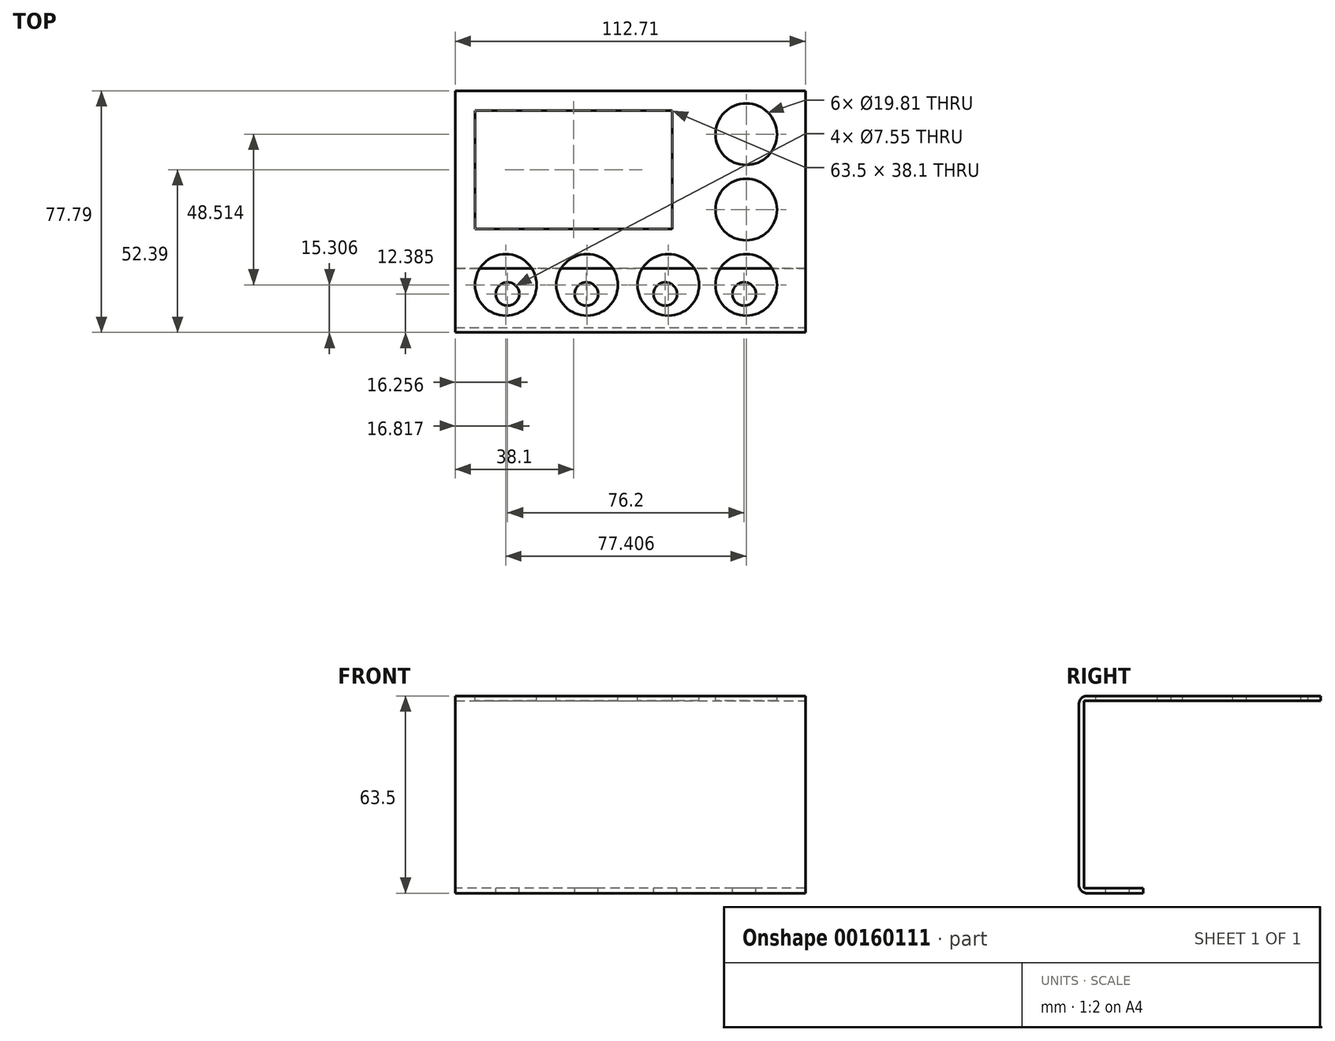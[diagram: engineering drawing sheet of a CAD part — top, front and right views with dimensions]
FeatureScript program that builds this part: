
annotation { "Feature Type Name" : "Feature", "Feature Type Description" : "" }
export const myFeature = defineFeature(function(context is Context, id is Id, definition is map)
    precondition{}
    {
        {
            var Q0;
            Q0=qCreatedBy(makeId("Top.planeOp"),FACE);
            var sketch = newSketch(context, id + "F0", { "sketchPlane" : qUnion([Q0])});
            skLineSegment(sketch, "E0.bottom", {"start": v(-56.35, 38.1) * mm, "end": v(56.36, 38.1) * mm});
            skLineSegment(sketch, "E0.top", {"start": v(-56.35, -38.1) * mm, "end": v(56.36, -38.1) * mm});
            skLineSegment(sketch, "E0.left", {"start": v(-56.35, 38.1) * mm, "end": v(-56.35, -38.1) * mm});
            skLineSegment(sketch, "E0.right", {"start": v(56.36, 38.1) * mm, "end": v(56.36, -38.1) * mm});
            skSolve(sketch);
        }
        {
            var Q0;
            Q0=makeQuery(id+"F0.imprint","IMPRINT",FACE,{"disambiguationData":[TD([[makeQuery(id+"F0.imprint","IMPRINT",EDGE,{"derivedFrom":sQuery(id+"F0.wireOp",EDGE,"E0.bottom")}),-1.0]])]});
            extrude(context, id + "F1", {"entities" : qUnion([Q0]), "depth" : 1.59 * mm});
        }
        {
            var Q0;
            Q0=makeQuery(id+"F1.opExtrude","CAP_FACE",FACE,{"disambiguationData":[OSD([sQuery(id+"F0.wireOp",EDGE,"E0.bottom"),sQuery(id+"F0.wireOp",EDGE,"E0.top"),sQuery(id+"F0.wireOp",EDGE,"E0.left"),sQuery(id+"F0.wireOp",EDGE,"E0.right")])],"isStart":false});
            var sketch = newSketch(context, id + "F2", { "sketchPlane" : qUnion([Q0])});
            skLineSegment(sketch, "E1.bottom", {"start": v(-50, 31.75) * mm, "end": v(13.5, 31.75) * mm});
            skLineSegment(sketch, "E1.top", {"start": v(-50, -6.35) * mm, "end": v(13.5, -6.35) * mm});
            skLineSegment(sketch, "E1.left", {"start": v(-50, 31.75) * mm, "end": v(-50, -6.35) * mm});
            skLineSegment(sketch, "E1.right", {"start": v(13.5, 31.75) * mm, "end": v(13.5, -6.35) * mm});
            skCircle(sketch, "E2", {"center": v(37.31, 24.13) * mm, "radius": 9.9 * mm});
            skCircle(sketch, "E3", {"center": v(37.31, -0.13) * mm, "radius": 9.9 * mm});
            skCircle(sketch, "E4", {"center": v(37.31, -24.38) * mm, "radius": 9.9 * mm});
            skLineSegment(sketch, "E5", {"start": v(37.31, 38.1) * mm, "end": v(37.31, -38.1) * mm, "construction": true});
            skLineSegment(sketch, "E6", {"start": v(37.31, -24.38) * mm, "end": v(-56.35, -24.38) * mm, "construction": true});
            skCircle(sketch, "E7", {"center": v(-40.1, -24.38) * mm, "radius": 9.9 * mm});
            skCircle(sketch, "E8", {"center": v(-13.93, -24.38) * mm, "radius": 9.9 * mm});
            skCircle(sketch, "E9", {"center": v(12.23, -24.38) * mm, "radius": 9.9 * mm});
            skSolve(sketch);
        }
        {
            var Q0;
            Q0 = qSketchRegion(id + "F2", true);
            extrude(context, id + "F3", {"entities" : qUnion([Q0]), "operationType" : NewBodyOperationType.REMOVE, "endBound" : BoundingType.THROUGH_ALL, "oppositeDirection" : true, "depth" : 25.4 * mm});
        }
        {
            var Q0;
            Q0=makeQuery(id+"F1.opExtrude","CAP_FACE",FACE,{"disambiguationData":[OSD([sQuery(id+"F0.wireOp",EDGE,"E0.bottom"),sQuery(id+"F0.wireOp",EDGE,"E0.top"),sQuery(id+"F0.wireOp",EDGE,"E0.left"),sQuery(id+"F0.wireOp",EDGE,"E0.right")])],"isStart":false});
            var sketch = newSketch(context, id + "F4", { "sketchPlane" : qUnion([Q0])});
            skLineSegment(sketch, "E10.bottom", {"start": v(-56.35, -38.1) * mm, "end": v(56.36, -38.1) * mm});
            skLineSegment(sketch, "E10.top", {"start": v(-56.35, -39.69) * mm, "end": v(56.36, -39.69) * mm});
            skLineSegment(sketch, "E10.left", {"start": v(-56.35, -38.1) * mm, "end": v(-56.35, -39.69) * mm});
            skLineSegment(sketch, "E10.right", {"start": v(56.36, -38.1) * mm, "end": v(56.36, -39.69) * mm});
            skSolve(sketch);
        }
        {
            var Q0;
            Q0 = qSketchRegion(id + "F4", true);
            extrude(context, id + "F5", {"entities" : qUnion([Q0]), "operationType" : NewBodyOperationType.ADD, "oppositeDirection" : true, "depth" : 63.5 * mm});
        }
        {
            var Q0;
            Q0=makeQuery(id+"F5.opExtrude","SWEPT_FACE",FACE,{"disambiguationData":[OSD([sQuery(id+"F4.wireOp",EDGE,"E10.bottom")])]});
            var sketch = newSketch(context, id + "F6", { "sketchPlane" : qUnion([Q0])});
            skLineSegment(sketch, "E11.bottom", {"start": v(-56.36, -61.91) * mm, "end": v(56.35, -61.91) * mm});
            skLineSegment(sketch, "E11.top", {"start": v(-56.36, -60.33) * mm, "end": v(56.35, -60.33) * mm});
            skLineSegment(sketch, "E11.left", {"start": v(-56.36, -61.91) * mm, "end": v(-56.36, -60.33) * mm});
            skLineSegment(sketch, "E11.right", {"start": v(56.35, -61.91) * mm, "end": v(56.35, -60.33) * mm});
            skSolve(sketch);
        }
        {
            var Q0;
            Q0 = qSketchRegion(id + "F6", true);
            extrude(context, id + "F7", {"entities" : qUnion([Q0]), "operationType" : NewBodyOperationType.ADD, "depth" : 19.05 * mm});
        }
        {
            var Q0;
            Q0=makeQuery(id+"F5.opExtrude","CAP_EDGE",EDGE,{"disambiguationData":[OSD([sQuery(id+"F4.wireOp",EDGE,"E10.top")])],"isStart":true});
            var Q1;
            Q1=makeQuery(id+"F1.opExtrude","CAP_EDGE",EDGE,{"disambiguationData":[OSD([sQuery(id+"F0.wireOp",EDGE,"E0.top")])],"isStart":true});
            var Q2;
            Q2=makeQuery(id+"F5.opExtrude","CAP_EDGE",EDGE,{"disambiguationData":[OSD([sQuery(id+"F4.wireOp",EDGE,"E10.top")])],"isStart":false});
            var Q3;
            Q3=makeQuery(id+"F7.opExtrude","CAP_EDGE",EDGE,{"disambiguationData":[OSD([sQuery(id+"F6.wireOp",EDGE,"E11.top")])],"isStart":true});
            fillet(context, id + "F8", {"entities" : qUnion([Q0, Q1, Q2, Q3]), "radius" : 2.54 * mm, "tangentPropagation" : true, "allowEdgeOverflow" : false});
        }
        {
            var Q0;
            Q0=makeQuery(id+"F7.opExtrude","SWEPT_FACE",FACE,{"disambiguationData":[OSD([sQuery(id+"F6.wireOp",EDGE,"E11.top")])]});
            var sketch = newSketch(context, id + "F9", { "sketchPlane" : qUnion([Q0])});
            skLineSegment(sketch, "E12", {"start": v(-56.35, -27.3) * mm, "end": v(56.36, -27.3) * mm, "construction": true});
            skCircle(sketch, "E13", {"center": v(-39.53, -27.3) * mm, "radius": 3.78 * mm});
            skCircle(sketch, "E14.1.0.0", {"center": v(-14.13, -27.3) * mm, "radius": 3.78 * mm});
            skCircle(sketch, "E14.2.0.0", {"center": v(11.27, -27.3) * mm, "radius": 3.78 * mm});
            skCircle(sketch, "E14.3.0.0", {"center": v(36.67, -27.3) * mm, "radius": 3.78 * mm});
            skLineSegment(sketch, "E14.direction1", {"start": v(-39.53, -27.3) * mm, "end": v(-14.13, -27.3) * mm, "construction": true});
            skSolve(sketch);
        }
        {
            var Q0;
            Q0 = qSketchRegion(id + "F9", true);
            extrude(context, id + "F10", {"entities" : qUnion([Q0]), "operationType" : NewBodyOperationType.REMOVE, "endBound" : BoundingType.THROUGH_ALL, "oppositeDirection" : true, "depth" : 25.4 * mm});
        }
    });
